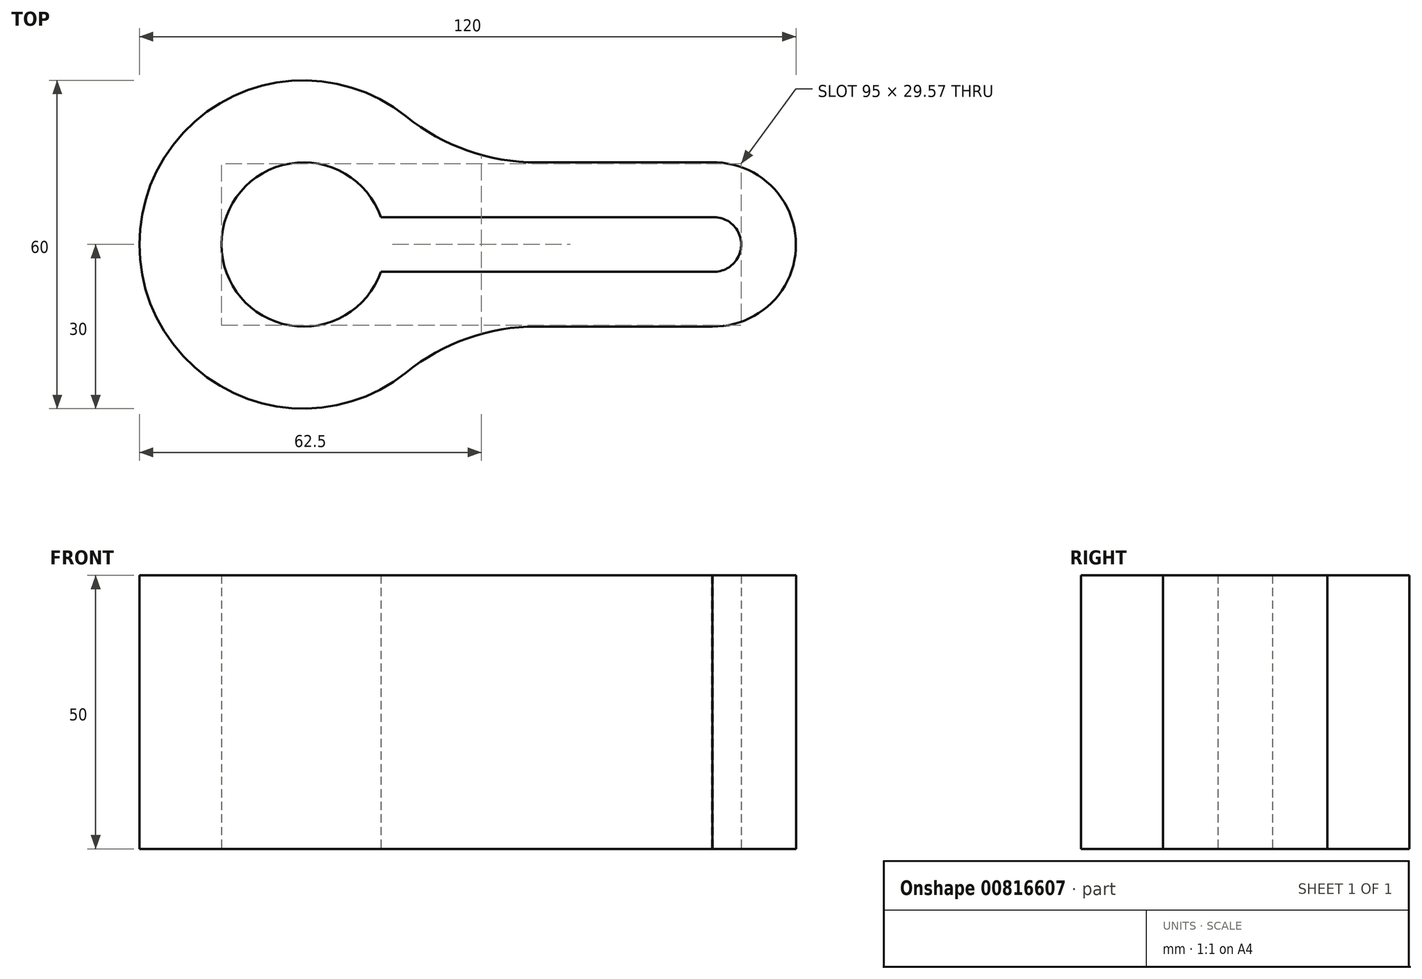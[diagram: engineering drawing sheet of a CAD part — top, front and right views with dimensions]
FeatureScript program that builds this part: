
annotation { "Feature Type Name" : "Feature", "Feature Type Description" : "" }
export const myFeature = defineFeature(function(context is Context, id is Id, definition is map)
    precondition{}
    {
        {
            var Q0;
            Q0=qCreatedBy(makeId("Top.planeOp"),FACE);
            var sketch = newSketch(context, id + "F0", { "sketchPlane" : qUnion([Q0])});
            skArc(sketch, "E0", {"start": v(14.14, 5) * mm, "mid": v(-15, 0) * mm, "end": v(14.14, -5) * mm});
            skArc(sketch, "E1", {"start": v(74.85, -5) * mm, "mid": v(80, 0.05) * mm, "end": v(74.75, 5) * mm});
            skLineSegment(sketch, "E2", {"start": v(75.25, 5) * mm, "end": v(14.14, 5) * mm});
            skLineSegment(sketch, "E3", {"start": v(74.85, -5) * mm, "end": v(14.14, -5) * mm});
            skArc(sketch, "E4", {"start": v(18.8, 23.38) * mm, "mid": v(-30, 0) * mm, "end": v(18.8, -23.38) * mm});
            skArc(sketch, "E5", {"start": v(74.7, -15) * mm, "mid": v(90, 0.09) * mm, "end": v(74.53, 15) * mm});
            skLineSegment(sketch, "E6", {"start": v(75.47, 15) * mm, "end": v(42.61, 15) * mm});
            skLineSegment(sketch, "E7", {"start": v(75.3, -15) * mm, "end": v(42.6, -15) * mm});
            skPoint(sketch, "E8.visualSharp", {"position": v(25.98, -15) * mm});
            skArc(sketch, "E8.filletArc", {"start": v(42.6, -15) * mm, "mid": v(29.99, -17.15) * mm, "end": v(18.8, -23.38) * mm});
            skPoint(sketch, "E9.visualSharp", {"position": v(25.99, 15) * mm});
            skArc(sketch, "E9.filletArc", {"start": v(18.8, 23.38) * mm, "mid": v(29.99, 17.15) * mm, "end": v(42.61, 15) * mm});
            skSolve(sketch);
        }
        {
            var Q0;
            Q0 = qSketchRegion(id + "F0", true);
            extrude(context, id + "F1", {"entities" : qUnion([Q0]), "depth" : 50 * mm, "offsetDistance" : 25 * mm});
        }
    });
